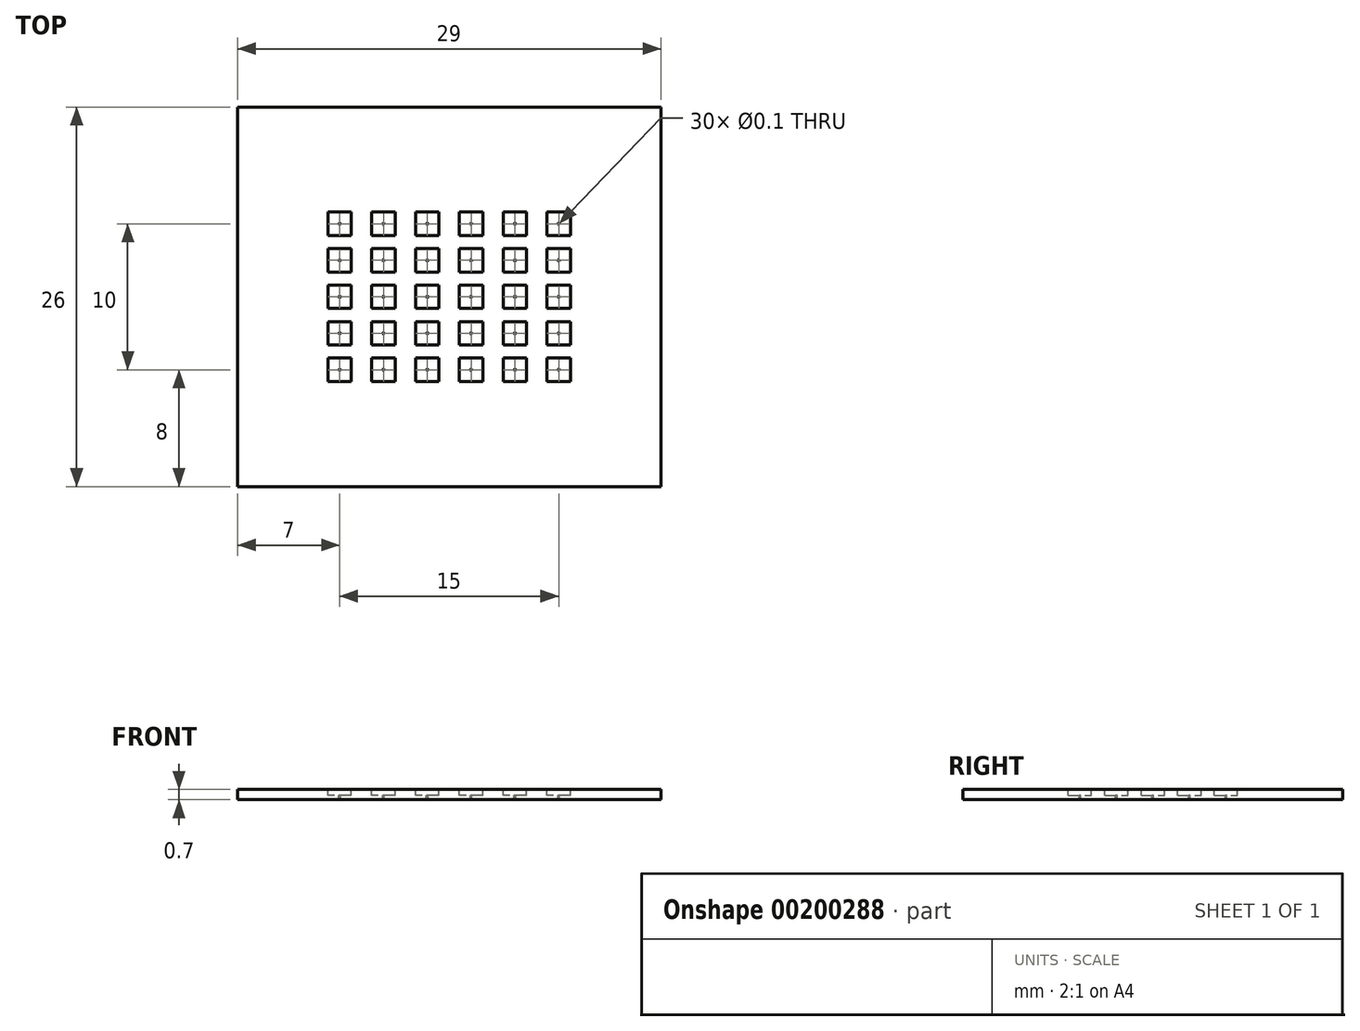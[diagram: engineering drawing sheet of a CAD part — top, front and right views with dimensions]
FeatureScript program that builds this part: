
annotation { "Feature Type Name" : "Feature", "Feature Type Description" : "" }
export const myFeature = defineFeature(function(context is Context, id is Id, definition is map)
    precondition{}
    {
        {
            var Q0;
            Q0=qCreatedBy(makeId("Top.planeOp"),FACE);
            var sketch = newSketch(context, id + "F0", { "sketchPlane" : qUnion([Q0])});
            skLineSegment(sketch, "E0.bottom", {"start": v(14.5, -13) * mm, "end": v(-14.5, -13) * mm});
            skLineSegment(sketch, "E0.top", {"start": v(14.5, 13) * mm, "end": v(-14.5, 13) * mm});
            skLineSegment(sketch, "E0.left", {"start": v(14.5, -13) * mm, "end": v(14.5, 13) * mm});
            skLineSegment(sketch, "E0.right", {"start": v(-14.5, -13) * mm, "end": v(-14.5, 13) * mm});
            skPoint(sketch, "E0.middle", {"position": v(0, 0) * mm});
            skSolve(sketch);
        }
        {
            var Q0;
            Q0=qSketchRegion(id+"F0",true);
            var Q1;
            Q1=makeQuery(id+"F0.imprint","IMPRINT",FACE,{"disambiguationData":[TD([[makeQuery(id+"F0.imprint","IMPRINT",EDGE,{"derivedFrom":sQuery(id+"F0.wireOp",EDGE,"UkhYZKIQ-UkVG-Lxvr-Lrxv-xQsFVOTcTfzZ.bottom")}),-1.0]])]});
            extrude(context, id + "F1", {"entities" : qUnion([Q0, Q1]), "oppositeDirection" : true, "depth" : 0.7 * mm});
        }
        {
            var Q0;
            Q0=makeQuery(id+"F1.opExtrude","CAP_FACE",FACE,{"disambiguationData":[OSD([sQuery(id+"F0.wireOp",EDGE,"E0.bottom"),sQuery(id+"F0.wireOp",EDGE,"E0.top"),sQuery(id+"F0.wireOp",EDGE,"E0.left"),sQuery(id+"F0.wireOp",EDGE,"E0.right")])],"isStart":true});
            var sketch = newSketch(context, id + "F2", { "sketchPlane" : qUnion([Q0])});
            skLineSegment(sketch, "E1.bottom", {"start": v(12.75, -11.25) * mm, "end": v(-12.75, -11.25) * mm});
            skLineSegment(sketch, "E1.top", {"start": v(12.75, 11.25) * mm, "end": v(-12.75, 11.25) * mm});
            skLineSegment(sketch, "E1.left", {"start": v(12.75, -11.25) * mm, "end": v(12.75, 11.25) * mm});
            skLineSegment(sketch, "E1.right", {"start": v(-12.75, -11.25) * mm, "end": v(-12.75, 11.25) * mm});
            skPoint(sketch, "E1.middle", {"position": v(0, 0) * mm});
            skLineSegment(sketch, "E2.bottom", {"start": v(13.25, -11.75) * mm, "end": v(-13.25, -11.75) * mm});
            skLineSegment(sketch, "E2.top", {"start": v(13.25, 11.75) * mm, "end": v(-13.25, 11.75) * mm});
            skLineSegment(sketch, "E2.left", {"start": v(13.25, -11.75) * mm, "end": v(13.25, 11.75) * mm});
            skLineSegment(sketch, "E2.right", {"start": v(-13.25, -11.75) * mm, "end": v(-13.25, 11.75) * mm});
            skSolve(sketch);
        }
        {
            var Q0;
            Q0=makeQuery(id+"FLxWal6u9J4FSth_1.boolean.opBoolean","SPLIT",FACE,{"disambiguationData":[TD([makeQuery(id+"FLxWal6u9J4FSth_1.opExtrude","SWEPT_FACE",FACE,{"disambiguationData":[OSD([sQuery(id+"F2.wireOp",EDGE,"E1.bottom")])]})])],"derivedFrom":makeQuery(id+"F1.opExtrude","CAP_FACE",FACE,{"disambiguationData":[OSD([sQuery(id+"F0.wireOp",EDGE,"E0.bottom"),sQuery(id+"F0.wireOp",EDGE,"E0.top"),sQuery(id+"F0.wireOp",EDGE,"E0.left"),sQuery(id+"F0.wireOp",EDGE,"E0.right")])],"isStart":true})});
            var sketch = newSketch(context, id + "F3", { "sketchPlane" : qUnion([Q0])});
            skPoint(sketch, "E3.middle", {"position": v(0, 0) * mm});
            skPoint(sketch, "E4", {"position": v(-7.5, 5) * mm});
            skPoint(sketch, "E5", {"position": v(-4.5, 5) * mm});
            skPoint(sketch, "E6", {"position": v(-1.5, 5) * mm});
            skPoint(sketch, "E7", {"position": v(1.5, 5) * mm});
            skPoint(sketch, "E8", {"position": v(4.5, 5) * mm});
            skPoint(sketch, "E9", {"position": v(7.5, 5) * mm});
            skPoint(sketch, "E10", {"position": v(-7.5, 2.5) * mm});
            skPoint(sketch, "E11", {"position": v(-4.5, 2.5) * mm});
            skPoint(sketch, "E12", {"position": v(-1.5, 2.5) * mm});
            skPoint(sketch, "E13", {"position": v(1.5, 2.5) * mm});
            skPoint(sketch, "E14", {"position": v(4.5, 2.5) * mm});
            skPoint(sketch, "E15", {"position": v(7.5, 2.5) * mm});
            skPoint(sketch, "E16", {"position": v(-7.5, 0) * mm});
            skPoint(sketch, "E17", {"position": v(-4.5, 0) * mm});
            skPoint(sketch, "E18", {"position": v(-1.5, 0) * mm});
            skPoint(sketch, "E19", {"position": v(1.5, 0) * mm});
            skPoint(sketch, "E20", {"position": v(4.5, 0) * mm});
            skPoint(sketch, "E21", {"position": v(7.5, 0) * mm});
            skPoint(sketch, "E22", {"position": v(-7.5, -2.5) * mm});
            skPoint(sketch, "E23", {"position": v(-4.5, -2.5) * mm});
            skPoint(sketch, "E24", {"position": v(-1.5, -2.5) * mm});
            skPoint(sketch, "E25", {"position": v(1.5, -2.5) * mm});
            skPoint(sketch, "E26", {"position": v(4.5, -2.5) * mm});
            skPoint(sketch, "E27", {"position": v(7.5, -2.5) * mm});
            skPoint(sketch, "E28", {"position": v(-7.5, -5) * mm});
            skPoint(sketch, "E29", {"position": v(-4.5, -5) * mm});
            skPoint(sketch, "E30", {"position": v(-1.5, -5) * mm});
            skPoint(sketch, "E31", {"position": v(1.5, -5) * mm});
            skPoint(sketch, "E32", {"position": v(4.5, -5) * mm});
            skPoint(sketch, "E33", {"position": v(7.5, -5) * mm});
            skLineSegment(sketch, "E34.bottom", {"start": v(-6.7, 4.2) * mm, "end": v(-8.3, 4.2) * mm});
            skLineSegment(sketch, "E34.top", {"start": v(-6.7, 5.8) * mm, "end": v(-8.3, 5.8) * mm});
            skLineSegment(sketch, "E34.left", {"start": v(-6.7, 4.2) * mm, "end": v(-6.7, 5.8) * mm});
            skLineSegment(sketch, "E34.right", {"start": v(-8.3, 4.2) * mm, "end": v(-8.3, 5.8) * mm});
            skLineSegment(sketch, "E35.bottom", {"start": v(-3.7, 4.2) * mm, "end": v(-5.3, 4.2) * mm});
            skLineSegment(sketch, "E35.top", {"start": v(-3.7, 5.8) * mm, "end": v(-5.3, 5.8) * mm});
            skLineSegment(sketch, "E35.left", {"start": v(-3.7, 4.2) * mm, "end": v(-3.7, 5.8) * mm});
            skLineSegment(sketch, "E35.right", {"start": v(-5.3, 4.2) * mm, "end": v(-5.3, 5.8) * mm});
            skLineSegment(sketch, "E36.bottom", {"start": v(-0.7, 4.2) * mm, "end": v(-2.3, 4.2) * mm});
            skLineSegment(sketch, "E36.top", {"start": v(-0.7, 5.8) * mm, "end": v(-2.3, 5.8) * mm});
            skLineSegment(sketch, "E36.left", {"start": v(-0.7, 4.2) * mm, "end": v(-0.7, 5.8) * mm});
            skLineSegment(sketch, "E36.right", {"start": v(-2.3, 4.2) * mm, "end": v(-2.3, 5.8) * mm});
            skLineSegment(sketch, "E37.bottom", {"start": v(2.3, 4.2) * mm, "end": v(0.7, 4.2) * mm});
            skLineSegment(sketch, "E37.top", {"start": v(2.3, 5.8) * mm, "end": v(0.7, 5.8) * mm});
            skLineSegment(sketch, "E37.left", {"start": v(2.3, 4.2) * mm, "end": v(2.3, 5.8) * mm});
            skLineSegment(sketch, "E37.right", {"start": v(0.7, 4.2) * mm, "end": v(0.7, 5.8) * mm});
            skLineSegment(sketch, "E38.bottom", {"start": v(5.3, 4.2) * mm, "end": v(3.7, 4.2) * mm});
            skLineSegment(sketch, "E38.top", {"start": v(5.3, 5.8) * mm, "end": v(3.7, 5.8) * mm});
            skLineSegment(sketch, "E38.left", {"start": v(5.3, 4.2) * mm, "end": v(5.3, 5.8) * mm});
            skLineSegment(sketch, "E38.right", {"start": v(3.7, 4.2) * mm, "end": v(3.7, 5.8) * mm});
            skLineSegment(sketch, "E39.bottom", {"start": v(8.3, 4.2) * mm, "end": v(6.7, 4.2) * mm});
            skLineSegment(sketch, "E39.top", {"start": v(8.3, 5.8) * mm, "end": v(6.7, 5.8) * mm});
            skLineSegment(sketch, "E39.left", {"start": v(8.3, 4.2) * mm, "end": v(8.3, 5.8) * mm});
            skLineSegment(sketch, "E39.right", {"start": v(6.7, 4.2) * mm, "end": v(6.7, 5.8) * mm});
            skLineSegment(sketch, "E40.bottom", {"start": v(-6.7, 1.7) * mm, "end": v(-8.3, 1.7) * mm});
            skLineSegment(sketch, "E40.top", {"start": v(-6.7, 3.3) * mm, "end": v(-8.3, 3.3) * mm});
            skLineSegment(sketch, "E40.left", {"start": v(-6.7, 1.7) * mm, "end": v(-6.7, 3.3) * mm});
            skLineSegment(sketch, "E40.right", {"start": v(-8.3, 1.7) * mm, "end": v(-8.3, 3.3) * mm});
            skLineSegment(sketch, "E41.bottom", {"start": v(-3.7, 1.7) * mm, "end": v(-5.3, 1.7) * mm});
            skLineSegment(sketch, "E41.top", {"start": v(-3.7, 3.3) * mm, "end": v(-5.3, 3.3) * mm});
            skLineSegment(sketch, "E41.left", {"start": v(-3.7, 1.7) * mm, "end": v(-3.7, 3.3) * mm});
            skLineSegment(sketch, "E41.right", {"start": v(-5.3, 1.7) * mm, "end": v(-5.3, 3.3) * mm});
            skLineSegment(sketch, "E42.bottom", {"start": v(-0.7, 1.7) * mm, "end": v(-2.3, 1.7) * mm});
            skLineSegment(sketch, "E42.top", {"start": v(-0.7, 3.3) * mm, "end": v(-2.3, 3.3) * mm});
            skLineSegment(sketch, "E42.left", {"start": v(-0.7, 1.7) * mm, "end": v(-0.7, 3.3) * mm});
            skLineSegment(sketch, "E42.right", {"start": v(-2.3, 1.7) * mm, "end": v(-2.3, 3.3) * mm});
            skLineSegment(sketch, "E43.bottom", {"start": v(2.3, 1.7) * mm, "end": v(0.7, 1.7) * mm});
            skLineSegment(sketch, "E43.top", {"start": v(2.3, 3.3) * mm, "end": v(0.7, 3.3) * mm});
            skLineSegment(sketch, "E43.left", {"start": v(2.3, 1.7) * mm, "end": v(2.3, 3.3) * mm});
            skLineSegment(sketch, "E43.right", {"start": v(0.7, 1.7) * mm, "end": v(0.7, 3.3) * mm});
            skLineSegment(sketch, "E44.bottom", {"start": v(5.3, 1.7) * mm, "end": v(3.7, 1.7) * mm});
            skLineSegment(sketch, "E44.top", {"start": v(5.3, 3.3) * mm, "end": v(3.7, 3.3) * mm});
            skLineSegment(sketch, "E44.left", {"start": v(5.3, 1.7) * mm, "end": v(5.3, 3.3) * mm});
            skLineSegment(sketch, "E44.right", {"start": v(3.7, 1.7) * mm, "end": v(3.7, 3.3) * mm});
            skLineSegment(sketch, "E45.bottom", {"start": v(8.3, 1.7) * mm, "end": v(6.7, 1.7) * mm});
            skLineSegment(sketch, "E45.top", {"start": v(8.3, 3.3) * mm, "end": v(6.7, 3.3) * mm});
            skLineSegment(sketch, "E45.left", {"start": v(8.3, 1.7) * mm, "end": v(8.3, 3.3) * mm});
            skLineSegment(sketch, "E45.right", {"start": v(6.7, 1.7) * mm, "end": v(6.7, 3.3) * mm});
            skLineSegment(sketch, "E46.bottom", {"start": v(-6.7, -0.8) * mm, "end": v(-8.3, -0.8) * mm});
            skLineSegment(sketch, "E46.top", {"start": v(-6.7, 0.8) * mm, "end": v(-8.3, 0.8) * mm});
            skLineSegment(sketch, "E46.left", {"start": v(-6.7, -0.8) * mm, "end": v(-6.7, 0.8) * mm});
            skLineSegment(sketch, "E46.right", {"start": v(-8.3, -0.8) * mm, "end": v(-8.3, 0.8) * mm});
            skLineSegment(sketch, "E47.bottom", {"start": v(-3.7, -0.8) * mm, "end": v(-5.3, -0.8) * mm});
            skLineSegment(sketch, "E47.top", {"start": v(-3.7, 0.8) * mm, "end": v(-5.3, 0.8) * mm});
            skLineSegment(sketch, "E47.left", {"start": v(-3.7, -0.8) * mm, "end": v(-3.7, 0.8) * mm});
            skLineSegment(sketch, "E47.right", {"start": v(-5.3, -0.8) * mm, "end": v(-5.3, 0.8) * mm});
            skLineSegment(sketch, "E48.bottom", {"start": v(-0.7, -0.8) * mm, "end": v(-2.3, -0.8) * mm});
            skLineSegment(sketch, "E48.top", {"start": v(-0.7, 0.8) * mm, "end": v(-2.3, 0.8) * mm});
            skLineSegment(sketch, "E48.left", {"start": v(-0.7, -0.8) * mm, "end": v(-0.7, 0.8) * mm});
            skLineSegment(sketch, "E48.right", {"start": v(-2.3, -0.8) * mm, "end": v(-2.3, 0.8) * mm});
            skLineSegment(sketch, "E49.bottom", {"start": v(2.3, -0.8) * mm, "end": v(0.7, -0.8) * mm});
            skLineSegment(sketch, "E49.top", {"start": v(2.3, 0.8) * mm, "end": v(0.7, 0.8) * mm});
            skLineSegment(sketch, "E49.left", {"start": v(2.3, -0.8) * mm, "end": v(2.3, 0.8) * mm});
            skLineSegment(sketch, "E49.right", {"start": v(0.7, -0.8) * mm, "end": v(0.7, 0.8) * mm});
            skLineSegment(sketch, "E50.bottom", {"start": v(5.3, -0.8) * mm, "end": v(3.7, -0.8) * mm});
            skLineSegment(sketch, "E50.top", {"start": v(5.3, 0.8) * mm, "end": v(3.7, 0.8) * mm});
            skLineSegment(sketch, "E50.left", {"start": v(5.3, -0.8) * mm, "end": v(5.3, 0.8) * mm});
            skLineSegment(sketch, "E50.right", {"start": v(3.7, -0.8) * mm, "end": v(3.7, 0.8) * mm});
            skLineSegment(sketch, "E51.bottom", {"start": v(8.3, -0.8) * mm, "end": v(6.7, -0.8) * mm});
            skLineSegment(sketch, "E51.top", {"start": v(8.3, 0.8) * mm, "end": v(6.7, 0.8) * mm});
            skLineSegment(sketch, "E51.left", {"start": v(8.3, -0.8) * mm, "end": v(8.3, 0.8) * mm});
            skLineSegment(sketch, "E51.right", {"start": v(6.7, -0.8) * mm, "end": v(6.7, 0.8) * mm});
            skLineSegment(sketch, "E52.bottom", {"start": v(-6.7, -3.3) * mm, "end": v(-8.3, -3.3) * mm});
            skLineSegment(sketch, "E52.top", {"start": v(-6.7, -1.7) * mm, "end": v(-8.3, -1.7) * mm});
            skLineSegment(sketch, "E52.left", {"start": v(-6.7, -3.3) * mm, "end": v(-6.7, -1.7) * mm});
            skLineSegment(sketch, "E52.right", {"start": v(-8.3, -3.3) * mm, "end": v(-8.3, -1.7) * mm});
            skLineSegment(sketch, "E53.bottom", {"start": v(-3.7, -3.3) * mm, "end": v(-5.3, -3.3) * mm});
            skLineSegment(sketch, "E53.top", {"start": v(-3.7, -1.7) * mm, "end": v(-5.3, -1.7) * mm});
            skLineSegment(sketch, "E53.left", {"start": v(-3.7, -3.3) * mm, "end": v(-3.7, -1.7) * mm});
            skLineSegment(sketch, "E53.right", {"start": v(-5.3, -3.3) * mm, "end": v(-5.3, -1.7) * mm});
            skLineSegment(sketch, "E54.bottom", {"start": v(-0.7, -3.3) * mm, "end": v(-2.3, -3.3) * mm});
            skLineSegment(sketch, "E54.top", {"start": v(-0.7, -1.7) * mm, "end": v(-2.3, -1.7) * mm});
            skLineSegment(sketch, "E54.left", {"start": v(-0.7, -3.3) * mm, "end": v(-0.7, -1.7) * mm});
            skLineSegment(sketch, "E54.right", {"start": v(-2.3, -3.3) * mm, "end": v(-2.3, -1.7) * mm});
            skLineSegment(sketch, "E55.bottom", {"start": v(2.3, -3.3) * mm, "end": v(0.7, -3.3) * mm});
            skLineSegment(sketch, "E55.top", {"start": v(2.3, -1.7) * mm, "end": v(0.7, -1.7) * mm});
            skLineSegment(sketch, "E55.left", {"start": v(2.3, -3.3) * mm, "end": v(2.3, -1.7) * mm});
            skLineSegment(sketch, "E55.right", {"start": v(0.7, -3.3) * mm, "end": v(0.7, -1.7) * mm});
            skLineSegment(sketch, "E56.bottom", {"start": v(5.3, -3.3) * mm, "end": v(3.7, -3.3) * mm});
            skLineSegment(sketch, "E56.top", {"start": v(5.3, -1.7) * mm, "end": v(3.7, -1.7) * mm});
            skLineSegment(sketch, "E56.left", {"start": v(5.3, -3.3) * mm, "end": v(5.3, -1.7) * mm});
            skLineSegment(sketch, "E56.right", {"start": v(3.7, -3.3) * mm, "end": v(3.7, -1.7) * mm});
            skLineSegment(sketch, "E57.bottom", {"start": v(8.3, -3.3) * mm, "end": v(6.7, -3.3) * mm});
            skLineSegment(sketch, "E57.top", {"start": v(8.3, -1.7) * mm, "end": v(6.7, -1.7) * mm});
            skLineSegment(sketch, "E57.left", {"start": v(8.3, -3.3) * mm, "end": v(8.3, -1.7) * mm});
            skLineSegment(sketch, "E57.right", {"start": v(6.7, -3.3) * mm, "end": v(6.7, -1.7) * mm});
            skLineSegment(sketch, "E58.bottom", {"start": v(-6.7, -5.8) * mm, "end": v(-8.3, -5.8) * mm});
            skLineSegment(sketch, "E58.top", {"start": v(-6.7, -4.2) * mm, "end": v(-8.3, -4.2) * mm});
            skLineSegment(sketch, "E58.left", {"start": v(-6.7, -5.8) * mm, "end": v(-6.7, -4.2) * mm});
            skLineSegment(sketch, "E58.right", {"start": v(-8.3, -5.8) * mm, "end": v(-8.3, -4.2) * mm});
            skLineSegment(sketch, "E59.bottom", {"start": v(-3.7, -5.8) * mm, "end": v(-5.3, -5.8) * mm});
            skLineSegment(sketch, "E59.top", {"start": v(-3.7, -4.2) * mm, "end": v(-5.3, -4.2) * mm});
            skLineSegment(sketch, "E59.left", {"start": v(-3.7, -5.8) * mm, "end": v(-3.7, -4.2) * mm});
            skLineSegment(sketch, "E59.right", {"start": v(-5.3, -5.8) * mm, "end": v(-5.3, -4.2) * mm});
            skLineSegment(sketch, "E60.bottom", {"start": v(-0.7, -5.8) * mm, "end": v(-2.3, -5.8) * mm});
            skLineSegment(sketch, "E60.top", {"start": v(-0.7, -4.2) * mm, "end": v(-2.3, -4.2) * mm});
            skLineSegment(sketch, "E60.left", {"start": v(-0.7, -5.8) * mm, "end": v(-0.7, -4.2) * mm});
            skLineSegment(sketch, "E60.right", {"start": v(-2.3, -5.8) * mm, "end": v(-2.3, -4.2) * mm});
            skLineSegment(sketch, "E61.bottom", {"start": v(2.3, -5.8) * mm, "end": v(0.7, -5.8) * mm});
            skLineSegment(sketch, "E61.top", {"start": v(2.3, -4.2) * mm, "end": v(0.7, -4.2) * mm});
            skLineSegment(sketch, "E61.left", {"start": v(2.3, -5.8) * mm, "end": v(2.3, -4.2) * mm});
            skLineSegment(sketch, "E61.right", {"start": v(0.7, -5.8) * mm, "end": v(0.7, -4.2) * mm});
            skLineSegment(sketch, "E62.bottom", {"start": v(5.3, -5.8) * mm, "end": v(3.7, -5.8) * mm});
            skLineSegment(sketch, "E62.top", {"start": v(5.3, -4.2) * mm, "end": v(3.7, -4.2) * mm});
            skLineSegment(sketch, "E62.left", {"start": v(5.3, -5.8) * mm, "end": v(5.3, -4.2) * mm});
            skLineSegment(sketch, "E62.right", {"start": v(3.7, -5.8) * mm, "end": v(3.7, -4.2) * mm});
            skLineSegment(sketch, "E63.bottom", {"start": v(8.3, -5.8) * mm, "end": v(6.7, -5.8) * mm});
            skLineSegment(sketch, "E63.top", {"start": v(8.3, -4.2) * mm, "end": v(6.7, -4.2) * mm});
            skLineSegment(sketch, "E63.left", {"start": v(8.3, -5.8) * mm, "end": v(8.3, -4.2) * mm});
            skLineSegment(sketch, "E63.right", {"start": v(6.7, -5.8) * mm, "end": v(6.7, -4.2) * mm});
            skSolve(sketch);
        }
        {
            var Q0;
            Q0=qSketchRegion(id+"F3",true);
            extrude(context, id + "F4", {"entities" : qUnion([Q0]), "operationType" : NewBodyOperationType.REMOVE, "oppositeDirection" : true, "depth" : 0.4 * mm, "offsetDistance" : 25 * mm});
        }
        {
            var Q0;
            Q0=makeQuery(id+"F4.boolean.opBoolean","COPY",FACE,{"derivedFrom":makeQuery(id+"F4.opExtrude","CAP_FACE",FACE,{"disambiguationData":[OSD([sQuery(id+"F3.wireOp",EDGE,"E34.bottom"),sQuery(id+"F3.wireOp",EDGE,"E34.top"),sQuery(id+"F3.wireOp",EDGE,"E34.left"),sQuery(id+"F3.wireOp",EDGE,"E34.right")])],"isStart":false})});
            var sketch = newSketch(context, id + "F5", { "sketchPlane" : qUnion([Q0])});
            skPoint(sketch, "E64", {"position": v(-7.5, 5) * mm});
            skSolve(sketch);
        }
        {
            var Q0;
            Q0=sQuery(id+"F5.wireOp",VERTEX,"E64");
            var Q1;
            Q1=makeQuery(id+"F1.opExtrude","SWEPT_BODY",BODY,{"disambiguationData":[OSD([sQuery(id+"F0.wireOp",EDGE,"E0.bottom"),sQuery(id+"F0.wireOp",EDGE,"E0.top"),sQuery(id+"F0.wireOp",EDGE,"E0.left"),sQuery(id+"F0.wireOp",EDGE,"E0.right")])]});
            hole(context, id + "F6", {"style" : HoleStyle.SIMPLE, "endStyle" : HoleEndStyle.THROUGH, "holeDiameter" : 0.1 * mm, "startFromSketch" : true, "locations" : qUnion([Q0]), "scope" : qUnion([Q1]), "isTappedThrough" : true});
        }
        {
            var Q0;
            Q0=makeQuery(id+"F4.boolean.opBoolean","COPY",FACE,{"derivedFrom":makeQuery(id+"F4.opExtrude","CAP_FACE",FACE,{"disambiguationData":[OSD([sQuery(id+"F3.wireOp",EDGE,"E35.bottom"),sQuery(id+"F3.wireOp",EDGE,"E35.top"),sQuery(id+"F3.wireOp",EDGE,"E35.left"),sQuery(id+"F3.wireOp",EDGE,"E35.right")])],"isStart":false})});
            var sketch = newSketch(context, id + "F7", { "sketchPlane" : qUnion([Q0])});
            skPoint(sketch, "E65", {"position": v(-4.5, 5) * mm});
            skSolve(sketch);
        }
        {
            var Q0;
            Q0=sQuery(id+"F7.wireOp",VERTEX,"E65");
            var Q1;
            Q1=makeQuery(id+"F1.opExtrude","SWEPT_BODY",BODY,{"disambiguationData":[OSD([sQuery(id+"F0.wireOp",EDGE,"E0.bottom"),sQuery(id+"F0.wireOp",EDGE,"E0.top"),sQuery(id+"F0.wireOp",EDGE,"E0.left"),sQuery(id+"F0.wireOp",EDGE,"E0.right")])]});
            hole(context, id + "F8", {"style" : HoleStyle.SIMPLE, "endStyle" : HoleEndStyle.THROUGH, "holeDiameter" : 0.1 * mm, "startFromSketch" : true, "locations" : qUnion([Q0]), "scope" : qUnion([Q1]), "isTappedThrough" : true});
        }
        {
            var Q0;
            Q0=makeQuery(id+"F4.boolean.opBoolean","COPY",FACE,{"derivedFrom":makeQuery(id+"F4.opExtrude","CAP_FACE",FACE,{"disambiguationData":[OSD([sQuery(id+"F3.wireOp",EDGE,"E36.bottom"),sQuery(id+"F3.wireOp",EDGE,"E36.top"),sQuery(id+"F3.wireOp",EDGE,"E36.left"),sQuery(id+"F3.wireOp",EDGE,"E36.right")])],"isStart":false})});
            var sketch = newSketch(context, id + "F9", { "sketchPlane" : qUnion([Q0])});
            skPoint(sketch, "E66", {"position": v(-1.5, 5) * mm});
            skSolve(sketch);
        }
        {
            var Q0;
            Q0=sQuery(id+"F9.wireOp",VERTEX,"E66");
            var Q1;
            Q1=makeQuery(id+"F1.opExtrude","SWEPT_BODY",BODY,{"disambiguationData":[OSD([sQuery(id+"F0.wireOp",EDGE,"E0.bottom"),sQuery(id+"F0.wireOp",EDGE,"E0.top"),sQuery(id+"F0.wireOp",EDGE,"E0.left"),sQuery(id+"F0.wireOp",EDGE,"E0.right")])]});
            hole(context, id + "F10", {"style" : HoleStyle.SIMPLE, "endStyle" : HoleEndStyle.THROUGH, "holeDiameter" : 0.1 * mm, "startFromSketch" : true, "locations" : qUnion([Q0]), "scope" : qUnion([Q1]), "isTappedThrough" : true});
        }
        {
            var Q0;
            Q0=makeQuery(id+"F4.boolean.opBoolean","COPY",FACE,{"derivedFrom":makeQuery(id+"F4.opExtrude","CAP_FACE",FACE,{"disambiguationData":[OSD([sQuery(id+"F3.wireOp",EDGE,"E37.bottom"),sQuery(id+"F3.wireOp",EDGE,"E37.top"),sQuery(id+"F3.wireOp",EDGE,"E37.left"),sQuery(id+"F3.wireOp",EDGE,"E37.right")])],"isStart":false})});
            var sketch = newSketch(context, id + "F11", { "sketchPlane" : qUnion([Q0])});
            skPoint(sketch, "E67", {"position": v(1.5, 5) * mm});
            skSolve(sketch);
        }
        {
            var Q0;
            Q0=sQuery(id+"F11.wireOp",VERTEX,"E67");
            var Q1;
            Q1=makeQuery(id+"F1.opExtrude","SWEPT_BODY",BODY,{"disambiguationData":[OSD([sQuery(id+"F0.wireOp",EDGE,"E0.bottom"),sQuery(id+"F0.wireOp",EDGE,"E0.top"),sQuery(id+"F0.wireOp",EDGE,"E0.left"),sQuery(id+"F0.wireOp",EDGE,"E0.right")])]});
            hole(context, id + "F12", {"style" : HoleStyle.SIMPLE, "endStyle" : HoleEndStyle.THROUGH, "holeDiameter" : 0.1 * mm, "startFromSketch" : true, "locations" : qUnion([Q0]), "scope" : qUnion([Q1]), "isTappedThrough" : true});
        }
        {
            var Q0;
            Q0=makeQuery(id+"F4.boolean.opBoolean","COPY",FACE,{"derivedFrom":makeQuery(id+"F4.opExtrude","CAP_FACE",FACE,{"disambiguationData":[OSD([sQuery(id+"F3.wireOp",EDGE,"E38.bottom"),sQuery(id+"F3.wireOp",EDGE,"E38.top"),sQuery(id+"F3.wireOp",EDGE,"E38.left"),sQuery(id+"F3.wireOp",EDGE,"E38.right")])],"isStart":false})});
            var sketch = newSketch(context, id + "F13", { "sketchPlane" : qUnion([Q0])});
            skPoint(sketch, "E68", {"position": v(4.5, 5) * mm});
            skSolve(sketch);
        }
        {
            var Q0;
            Q0=sQuery(id+"F13.wireOp",VERTEX,"E68");
            var Q1;
            Q1=makeQuery(id+"F1.opExtrude","SWEPT_BODY",BODY,{"disambiguationData":[OSD([sQuery(id+"F0.wireOp",EDGE,"E0.bottom"),sQuery(id+"F0.wireOp",EDGE,"E0.top"),sQuery(id+"F0.wireOp",EDGE,"E0.left"),sQuery(id+"F0.wireOp",EDGE,"E0.right")])]});
            hole(context, id + "F14", {"style" : HoleStyle.SIMPLE, "endStyle" : HoleEndStyle.THROUGH, "holeDiameter" : 0.1 * mm, "startFromSketch" : true, "locations" : qUnion([Q0]), "scope" : qUnion([Q1]), "isTappedThrough" : true});
        }
        {
            var Q0;
            Q0=makeQuery(id+"F4.boolean.opBoolean","COPY",FACE,{"derivedFrom":makeQuery(id+"F4.opExtrude","CAP_FACE",FACE,{"disambiguationData":[OSD([sQuery(id+"F3.wireOp",EDGE,"E39.bottom"),sQuery(id+"F3.wireOp",EDGE,"E39.top"),sQuery(id+"F3.wireOp",EDGE,"E39.left"),sQuery(id+"F3.wireOp",EDGE,"E39.right")])],"isStart":false})});
            var sketch = newSketch(context, id + "F15", { "sketchPlane" : qUnion([Q0])});
            skPoint(sketch, "E69", {"position": v(7.5, 5) * mm});
            skSolve(sketch);
        }
        {
            var Q0;
            Q0=sQuery(id+"F15.wireOp",VERTEX,"E69");
            var Q1;
            Q1=makeQuery(id+"F1.opExtrude","SWEPT_BODY",BODY,{"disambiguationData":[OSD([sQuery(id+"F0.wireOp",EDGE,"E0.bottom"),sQuery(id+"F0.wireOp",EDGE,"E0.top"),sQuery(id+"F0.wireOp",EDGE,"E0.left"),sQuery(id+"F0.wireOp",EDGE,"E0.right")])]});
            hole(context, id + "F16", {"style" : HoleStyle.SIMPLE, "endStyle" : HoleEndStyle.THROUGH, "holeDiameter" : 0.1 * mm, "startFromSketch" : true, "locations" : qUnion([Q0]), "scope" : qUnion([Q1]), "isTappedThrough" : true});
        }
        {
            var Q0;
            Q0=makeQuery(id+"F4.boolean.opBoolean","COPY",FACE,{"derivedFrom":makeQuery(id+"F4.opExtrude","CAP_FACE",FACE,{"disambiguationData":[OSD([sQuery(id+"F3.wireOp",EDGE,"E45.bottom"),sQuery(id+"F3.wireOp",EDGE,"E45.top"),sQuery(id+"F3.wireOp",EDGE,"E45.left"),sQuery(id+"F3.wireOp",EDGE,"E45.right")])],"isStart":false})});
            var sketch = newSketch(context, id + "F17", { "sketchPlane" : qUnion([Q0])});
            skPoint(sketch, "E70", {"position": v(7.5, 2.5) * mm});
            skSolve(sketch);
        }
        {
            var Q0;
            Q0=sQuery(id+"F17.wireOp",VERTEX,"E70");
            var Q1;
            Q1=makeQuery(id+"F1.opExtrude","SWEPT_BODY",BODY,{"disambiguationData":[OSD([sQuery(id+"F0.wireOp",EDGE,"E0.bottom"),sQuery(id+"F0.wireOp",EDGE,"E0.top"),sQuery(id+"F0.wireOp",EDGE,"E0.left"),sQuery(id+"F0.wireOp",EDGE,"E0.right")])]});
            hole(context, id + "F18", {"style" : HoleStyle.SIMPLE, "endStyle" : HoleEndStyle.THROUGH, "holeDiameter" : 0.1 * mm, "startFromSketch" : true, "locations" : qUnion([Q0]), "scope" : qUnion([Q1]), "isTappedThrough" : true});
        }
        {
            var Q0;
            Q0=makeQuery(id+"F4.boolean.opBoolean","COPY",FACE,{"derivedFrom":makeQuery(id+"F4.opExtrude","CAP_FACE",FACE,{"disambiguationData":[OSD([sQuery(id+"F3.wireOp",EDGE,"E44.bottom"),sQuery(id+"F3.wireOp",EDGE,"E44.top"),sQuery(id+"F3.wireOp",EDGE,"E44.left"),sQuery(id+"F3.wireOp",EDGE,"E44.right")])],"isStart":false})});
            var sketch = newSketch(context, id + "F19", { "sketchPlane" : qUnion([Q0])});
            skPoint(sketch, "E71", {"position": v(4.5, 2.5) * mm});
            skSolve(sketch);
        }
        {
            var Q0;
            Q0=sQuery(id+"F19.wireOp",VERTEX,"E71");
            var Q1;
            Q1=makeQuery(id+"F1.opExtrude","SWEPT_BODY",BODY,{"disambiguationData":[OSD([sQuery(id+"F0.wireOp",EDGE,"E0.bottom"),sQuery(id+"F0.wireOp",EDGE,"E0.top"),sQuery(id+"F0.wireOp",EDGE,"E0.left"),sQuery(id+"F0.wireOp",EDGE,"E0.right")])]});
            hole(context, id + "F20", {"style" : HoleStyle.SIMPLE, "endStyle" : HoleEndStyle.THROUGH, "holeDiameter" : 0.1 * mm, "startFromSketch" : true, "locations" : qUnion([Q0]), "scope" : qUnion([Q1]), "isTappedThrough" : true});
        }
        {
            var Q0;
            Q0=makeQuery(id+"F4.boolean.opBoolean","COPY",FACE,{"derivedFrom":makeQuery(id+"F4.opExtrude","CAP_FACE",FACE,{"disambiguationData":[OSD([sQuery(id+"F3.wireOp",EDGE,"E43.bottom"),sQuery(id+"F3.wireOp",EDGE,"E43.top"),sQuery(id+"F3.wireOp",EDGE,"E43.left"),sQuery(id+"F3.wireOp",EDGE,"E43.right")])],"isStart":false})});
            var sketch = newSketch(context, id + "F21", { "sketchPlane" : qUnion([Q0])});
            skPoint(sketch, "E72", {"position": v(1.5, 2.5) * mm});
            skSolve(sketch);
        }
        {
            var Q0;
            Q0=sQuery(id+"F21.wireOp",VERTEX,"E72");
            var Q1;
            Q1=makeQuery(id+"F1.opExtrude","SWEPT_BODY",BODY,{"disambiguationData":[OSD([sQuery(id+"F0.wireOp",EDGE,"E0.bottom"),sQuery(id+"F0.wireOp",EDGE,"E0.top"),sQuery(id+"F0.wireOp",EDGE,"E0.left"),sQuery(id+"F0.wireOp",EDGE,"E0.right")])]});
            hole(context, id + "F22", {"style" : HoleStyle.SIMPLE, "endStyle" : HoleEndStyle.THROUGH, "holeDiameter" : 0.1 * mm, "startFromSketch" : true, "locations" : qUnion([Q0]), "scope" : qUnion([Q1]), "isTappedThrough" : true});
        }
        {
            var Q0;
            Q0=makeQuery(id+"F4.boolean.opBoolean","COPY",FACE,{"derivedFrom":makeQuery(id+"F4.opExtrude","CAP_FACE",FACE,{"disambiguationData":[OSD([sQuery(id+"F3.wireOp",EDGE,"E42.bottom"),sQuery(id+"F3.wireOp",EDGE,"E42.top"),sQuery(id+"F3.wireOp",EDGE,"E42.left"),sQuery(id+"F3.wireOp",EDGE,"E42.right")])],"isStart":false})});
            var sketch = newSketch(context, id + "F23", { "sketchPlane" : qUnion([Q0])});
            skPoint(sketch, "E73", {"position": v(-1.5, 2.5) * mm});
            skSolve(sketch);
        }
        {
            var Q0;
            Q0=sQuery(id+"F23.wireOp",VERTEX,"E73");
            var Q1;
            Q1=makeQuery(id+"F1.opExtrude","SWEPT_BODY",BODY,{"disambiguationData":[OSD([sQuery(id+"F0.wireOp",EDGE,"E0.bottom"),sQuery(id+"F0.wireOp",EDGE,"E0.top"),sQuery(id+"F0.wireOp",EDGE,"E0.left"),sQuery(id+"F0.wireOp",EDGE,"E0.right")])]});
            hole(context, id + "F24", {"style" : HoleStyle.SIMPLE, "endStyle" : HoleEndStyle.THROUGH, "holeDiameter" : 0.1 * mm, "startFromSketch" : true, "locations" : qUnion([Q0]), "scope" : qUnion([Q1]), "isTappedThrough" : true});
        }
        {
            var Q0;
            Q0=makeQuery(id+"F4.boolean.opBoolean","COPY",FACE,{"derivedFrom":makeQuery(id+"F4.opExtrude","CAP_FACE",FACE,{"disambiguationData":[OSD([sQuery(id+"F3.wireOp",EDGE,"E41.bottom"),sQuery(id+"F3.wireOp",EDGE,"E41.top"),sQuery(id+"F3.wireOp",EDGE,"E41.left"),sQuery(id+"F3.wireOp",EDGE,"E41.right")])],"isStart":false})});
            var sketch = newSketch(context, id + "F25", { "sketchPlane" : qUnion([Q0])});
            skPoint(sketch, "E74", {"position": v(-4.5, 2.5) * mm});
            skSolve(sketch);
        }
        {
            var Q0;
            Q0=sQuery(id+"F25.wireOp",VERTEX,"E74");
            var Q1;
            Q1=makeQuery(id+"F1.opExtrude","SWEPT_BODY",BODY,{"disambiguationData":[OSD([sQuery(id+"F0.wireOp",EDGE,"E0.bottom"),sQuery(id+"F0.wireOp",EDGE,"E0.top"),sQuery(id+"F0.wireOp",EDGE,"E0.left"),sQuery(id+"F0.wireOp",EDGE,"E0.right")])]});
            hole(context, id + "F26", {"style" : HoleStyle.SIMPLE, "endStyle" : HoleEndStyle.THROUGH, "holeDiameter" : 0.1 * mm, "startFromSketch" : true, "locations" : qUnion([Q0]), "scope" : qUnion([Q1]), "isTappedThrough" : true});
        }
        {
            var Q0;
            Q0=makeQuery(id+"F4.boolean.opBoolean","COPY",FACE,{"derivedFrom":makeQuery(id+"F4.opExtrude","CAP_FACE",FACE,{"disambiguationData":[OSD([sQuery(id+"F3.wireOp",EDGE,"E40.bottom"),sQuery(id+"F3.wireOp",EDGE,"E40.top"),sQuery(id+"F3.wireOp",EDGE,"E40.left"),sQuery(id+"F3.wireOp",EDGE,"E40.right")])],"isStart":false})});
            var sketch = newSketch(context, id + "F27", { "sketchPlane" : qUnion([Q0])});
            skPoint(sketch, "E75", {"position": v(-7.5, 2.5) * mm});
            skSolve(sketch);
        }
        {
            var Q0;
            Q0=sQuery(id+"F27.wireOp",VERTEX,"E75");
            var Q1;
            Q1=makeQuery(id+"F1.opExtrude","SWEPT_BODY",BODY,{"disambiguationData":[OSD([sQuery(id+"F0.wireOp",EDGE,"E0.bottom"),sQuery(id+"F0.wireOp",EDGE,"E0.top"),sQuery(id+"F0.wireOp",EDGE,"E0.left"),sQuery(id+"F0.wireOp",EDGE,"E0.right")])]});
            hole(context, id + "F28", {"style" : HoleStyle.SIMPLE, "endStyle" : HoleEndStyle.THROUGH, "holeDiameter" : 0.1 * mm, "startFromSketch" : true, "locations" : qUnion([Q0]), "scope" : qUnion([Q1]), "isTappedThrough" : true});
        }
        {
            var Q0;
            Q0=makeQuery(id+"F4.boolean.opBoolean","COPY",FACE,{"derivedFrom":makeQuery(id+"F4.opExtrude","CAP_FACE",FACE,{"disambiguationData":[OSD([sQuery(id+"F3.wireOp",EDGE,"E46.bottom"),sQuery(id+"F3.wireOp",EDGE,"E46.top"),sQuery(id+"F3.wireOp",EDGE,"E46.left"),sQuery(id+"F3.wireOp",EDGE,"E46.right")])],"isStart":false})});
            var sketch = newSketch(context, id + "F29", { "sketchPlane" : qUnion([Q0])});
            skPoint(sketch, "E76", {"position": v(-7.5, 0) * mm});
            skSolve(sketch);
        }
        {
            var Q0;
            Q0=sQuery(id+"F29.wireOp",VERTEX,"E76");
            var Q1;
            Q1=makeQuery(id+"F1.opExtrude","SWEPT_BODY",BODY,{"disambiguationData":[OSD([sQuery(id+"F0.wireOp",EDGE,"E0.bottom"),sQuery(id+"F0.wireOp",EDGE,"E0.top"),sQuery(id+"F0.wireOp",EDGE,"E0.left"),sQuery(id+"F0.wireOp",EDGE,"E0.right")])]});
            hole(context, id + "F30", {"style" : HoleStyle.SIMPLE, "endStyle" : HoleEndStyle.THROUGH, "holeDiameter" : 0.1 * mm, "startFromSketch" : true, "locations" : qUnion([Q0]), "scope" : qUnion([Q1]), "isTappedThrough" : true});
        }
        {
            var Q0;
            Q0=makeQuery(id+"F4.boolean.opBoolean","COPY",FACE,{"derivedFrom":makeQuery(id+"F4.opExtrude","CAP_FACE",FACE,{"disambiguationData":[OSD([sQuery(id+"F3.wireOp",EDGE,"E47.bottom"),sQuery(id+"F3.wireOp",EDGE,"E47.top"),sQuery(id+"F3.wireOp",EDGE,"E47.left"),sQuery(id+"F3.wireOp",EDGE,"E47.right")])],"isStart":false})});
            var sketch = newSketch(context, id + "F31", { "sketchPlane" : qUnion([Q0])});
            skPoint(sketch, "E77", {"position": v(-4.5, 0) * mm});
            skSolve(sketch);
        }
        {
            var Q0;
            Q0=sQuery(id+"F31.wireOp",VERTEX,"E77");
            var Q1;
            Q1=makeQuery(id+"F1.opExtrude","SWEPT_BODY",BODY,{"disambiguationData":[OSD([sQuery(id+"F0.wireOp",EDGE,"E0.bottom"),sQuery(id+"F0.wireOp",EDGE,"E0.top"),sQuery(id+"F0.wireOp",EDGE,"E0.left"),sQuery(id+"F0.wireOp",EDGE,"E0.right")])]});
            hole(context, id + "F32", {"style" : HoleStyle.SIMPLE, "endStyle" : HoleEndStyle.THROUGH, "holeDiameter" : 0.1 * mm, "startFromSketch" : true, "locations" : qUnion([Q0]), "scope" : qUnion([Q1]), "isTappedThrough" : true});
        }
        {
            var Q0;
            Q0=makeQuery(id+"F4.boolean.opBoolean","COPY",FACE,{"derivedFrom":makeQuery(id+"F4.opExtrude","CAP_FACE",FACE,{"disambiguationData":[OSD([sQuery(id+"F3.wireOp",EDGE,"E48.bottom"),sQuery(id+"F3.wireOp",EDGE,"E48.top"),sQuery(id+"F3.wireOp",EDGE,"E48.left"),sQuery(id+"F3.wireOp",EDGE,"E48.right")])],"isStart":false})});
            var sketch = newSketch(context, id + "F33", { "sketchPlane" : qUnion([Q0])});
            skPoint(sketch, "E78", {"position": v(-1.5, 0) * mm});
            skSolve(sketch);
        }
        {
            var Q0;
            Q0=sQuery(id+"F33.wireOp",VERTEX,"E78");
            var Q1;
            Q1=makeQuery(id+"F1.opExtrude","SWEPT_BODY",BODY,{"disambiguationData":[OSD([sQuery(id+"F0.wireOp",EDGE,"E0.bottom"),sQuery(id+"F0.wireOp",EDGE,"E0.top"),sQuery(id+"F0.wireOp",EDGE,"E0.left"),sQuery(id+"F0.wireOp",EDGE,"E0.right")])]});
            hole(context, id + "F34", {"style" : HoleStyle.SIMPLE, "endStyle" : HoleEndStyle.THROUGH, "holeDiameter" : 0.1 * mm, "startFromSketch" : true, "locations" : qUnion([Q0]), "scope" : qUnion([Q1]), "isTappedThrough" : true});
        }
        {
            var Q0;
            Q0=makeQuery(id+"F4.boolean.opBoolean","COPY",FACE,{"derivedFrom":makeQuery(id+"F4.opExtrude","CAP_FACE",FACE,{"disambiguationData":[OSD([sQuery(id+"F3.wireOp",EDGE,"E49.bottom"),sQuery(id+"F3.wireOp",EDGE,"E49.top"),sQuery(id+"F3.wireOp",EDGE,"E49.left"),sQuery(id+"F3.wireOp",EDGE,"E49.right")])],"isStart":false})});
            var sketch = newSketch(context, id + "F35", { "sketchPlane" : qUnion([Q0])});
            skPoint(sketch, "E79", {"position": v(1.5, 0) * mm});
            skSolve(sketch);
        }
        {
            var Q0;
            Q0=sQuery(id+"F35.wireOp",VERTEX,"E79");
            var Q1;
            Q1=makeQuery(id+"F1.opExtrude","SWEPT_BODY",BODY,{"disambiguationData":[OSD([sQuery(id+"F0.wireOp",EDGE,"E0.bottom"),sQuery(id+"F0.wireOp",EDGE,"E0.top"),sQuery(id+"F0.wireOp",EDGE,"E0.left"),sQuery(id+"F0.wireOp",EDGE,"E0.right")])]});
            hole(context, id + "F36", {"style" : HoleStyle.SIMPLE, "endStyle" : HoleEndStyle.THROUGH, "holeDiameter" : 0.1 * mm, "startFromSketch" : true, "locations" : qUnion([Q0]), "scope" : qUnion([Q1]), "isTappedThrough" : true});
        }
        {
            var Q0;
            Q0=makeQuery(id+"F4.boolean.opBoolean","COPY",FACE,{"derivedFrom":makeQuery(id+"F4.opExtrude","CAP_FACE",FACE,{"disambiguationData":[OSD([sQuery(id+"F3.wireOp",EDGE,"E50.bottom"),sQuery(id+"F3.wireOp",EDGE,"E50.top"),sQuery(id+"F3.wireOp",EDGE,"E50.left"),sQuery(id+"F3.wireOp",EDGE,"E50.right")])],"isStart":false})});
            var sketch = newSketch(context, id + "F37", { "sketchPlane" : qUnion([Q0])});
            skPoint(sketch, "E80", {"position": v(4.5, 0) * mm});
            skSolve(sketch);
        }
        {
            var Q0;
            Q0=sQuery(id+"F37.wireOp",VERTEX,"E80");
            var Q1;
            Q1=makeQuery(id+"F1.opExtrude","SWEPT_BODY",BODY,{"disambiguationData":[OSD([sQuery(id+"F0.wireOp",EDGE,"E0.bottom"),sQuery(id+"F0.wireOp",EDGE,"E0.top"),sQuery(id+"F0.wireOp",EDGE,"E0.left"),sQuery(id+"F0.wireOp",EDGE,"E0.right")])]});
            hole(context, id + "F38", {"style" : HoleStyle.SIMPLE, "endStyle" : HoleEndStyle.THROUGH, "holeDiameter" : 0.1 * mm, "startFromSketch" : true, "locations" : qUnion([Q0]), "scope" : qUnion([Q1]), "isTappedThrough" : true});
        }
        {
            var Q0;
            Q0=makeQuery(id+"F4.boolean.opBoolean","COPY",FACE,{"derivedFrom":makeQuery(id+"F4.opExtrude","CAP_FACE",FACE,{"disambiguationData":[OSD([sQuery(id+"F3.wireOp",EDGE,"E51.bottom"),sQuery(id+"F3.wireOp",EDGE,"E51.top"),sQuery(id+"F3.wireOp",EDGE,"E51.left"),sQuery(id+"F3.wireOp",EDGE,"E51.right")])],"isStart":false})});
            var sketch = newSketch(context, id + "F39", { "sketchPlane" : qUnion([Q0])});
            skPoint(sketch, "E81", {"position": v(7.5, 0) * mm});
            skSolve(sketch);
        }
        {
            var Q0;
            Q0=sQuery(id+"F39.wireOp",VERTEX,"E81");
            var Q1;
            Q1=makeQuery(id+"F1.opExtrude","SWEPT_BODY",BODY,{"disambiguationData":[OSD([sQuery(id+"F0.wireOp",EDGE,"E0.bottom"),sQuery(id+"F0.wireOp",EDGE,"E0.top"),sQuery(id+"F0.wireOp",EDGE,"E0.left"),sQuery(id+"F0.wireOp",EDGE,"E0.right")])]});
            hole(context, id + "F40", {"style" : HoleStyle.SIMPLE, "endStyle" : HoleEndStyle.THROUGH, "holeDiameter" : 0.1 * mm, "startFromSketch" : true, "locations" : qUnion([Q0]), "scope" : qUnion([Q1]), "isTappedThrough" : true});
        }
        {
            var Q0;
            Q0=makeQuery(id+"F4.boolean.opBoolean","COPY",FACE,{"derivedFrom":makeQuery(id+"F4.opExtrude","CAP_FACE",FACE,{"disambiguationData":[OSD([sQuery(id+"F3.wireOp",EDGE,"E52.bottom"),sQuery(id+"F3.wireOp",EDGE,"E52.top"),sQuery(id+"F3.wireOp",EDGE,"E52.left"),sQuery(id+"F3.wireOp",EDGE,"E52.right")])],"isStart":false})});
            var sketch = newSketch(context, id + "F41", { "sketchPlane" : qUnion([Q0])});
            skPoint(sketch, "E82", {"position": v(-7.5, -2.5) * mm});
            skSolve(sketch);
        }
        {
            var Q0;
            Q0=sQuery(id+"F41.wireOp",VERTEX,"E82");
            var Q1;
            Q1=makeQuery(id+"F1.opExtrude","SWEPT_BODY",BODY,{"disambiguationData":[OSD([sQuery(id+"F0.wireOp",EDGE,"E0.bottom"),sQuery(id+"F0.wireOp",EDGE,"E0.top"),sQuery(id+"F0.wireOp",EDGE,"E0.left"),sQuery(id+"F0.wireOp",EDGE,"E0.right")])]});
            hole(context, id + "F42", {"style" : HoleStyle.SIMPLE, "endStyle" : HoleEndStyle.THROUGH, "holeDiameter" : 0.1 * mm, "startFromSketch" : true, "locations" : qUnion([Q0]), "scope" : qUnion([Q1]), "isTappedThrough" : true});
        }
        {
            var Q0;
            Q0=makeQuery(id+"F4.boolean.opBoolean","COPY",FACE,{"derivedFrom":makeQuery(id+"F4.opExtrude","CAP_FACE",FACE,{"disambiguationData":[OSD([sQuery(id+"F3.wireOp",EDGE,"E53.bottom"),sQuery(id+"F3.wireOp",EDGE,"E53.top"),sQuery(id+"F3.wireOp",EDGE,"E53.left"),sQuery(id+"F3.wireOp",EDGE,"E53.right")])],"isStart":false})});
            var sketch = newSketch(context, id + "F43", { "sketchPlane" : qUnion([Q0])});
            skPoint(sketch, "E83", {"position": v(-4.5, -2.5) * mm});
            skSolve(sketch);
        }
        {
            var Q0;
            Q0=sQuery(id+"F43.wireOp",VERTEX,"E83");
            var Q1;
            Q1=makeQuery(id+"F1.opExtrude","SWEPT_BODY",BODY,{"disambiguationData":[OSD([sQuery(id+"F0.wireOp",EDGE,"E0.bottom"),sQuery(id+"F0.wireOp",EDGE,"E0.top"),sQuery(id+"F0.wireOp",EDGE,"E0.left"),sQuery(id+"F0.wireOp",EDGE,"E0.right")])]});
            hole(context, id + "F44", {"style" : HoleStyle.SIMPLE, "endStyle" : HoleEndStyle.THROUGH, "holeDiameter" : 0.1 * mm, "startFromSketch" : true, "locations" : qUnion([Q0]), "scope" : qUnion([Q1]), "isTappedThrough" : true});
        }
        {
            var Q0;
            Q0=makeQuery(id+"F4.boolean.opBoolean","COPY",FACE,{"derivedFrom":makeQuery(id+"F4.opExtrude","CAP_FACE",FACE,{"disambiguationData":[OSD([sQuery(id+"F3.wireOp",EDGE,"E54.bottom"),sQuery(id+"F3.wireOp",EDGE,"E54.top"),sQuery(id+"F3.wireOp",EDGE,"E54.left"),sQuery(id+"F3.wireOp",EDGE,"E54.right")])],"isStart":false})});
            var sketch = newSketch(context, id + "F45", { "sketchPlane" : qUnion([Q0])});
            skPoint(sketch, "E84", {"position": v(-1.5, -2.5) * mm});
            skSolve(sketch);
        }
        {
            var Q0;
            Q0=sQuery(id+"F45.wireOp",VERTEX,"E84");
            var Q1;
            Q1=makeQuery(id+"F1.opExtrude","SWEPT_BODY",BODY,{"disambiguationData":[OSD([sQuery(id+"F0.wireOp",EDGE,"E0.bottom"),sQuery(id+"F0.wireOp",EDGE,"E0.top"),sQuery(id+"F0.wireOp",EDGE,"E0.left"),sQuery(id+"F0.wireOp",EDGE,"E0.right")])]});
            hole(context, id + "F46", {"style" : HoleStyle.SIMPLE, "endStyle" : HoleEndStyle.THROUGH, "holeDiameter" : 0.1 * mm, "startFromSketch" : true, "locations" : qUnion([Q0]), "scope" : qUnion([Q1]), "isTappedThrough" : true});
        }
        {
            var Q0;
            Q0=makeQuery(id+"F4.boolean.opBoolean","COPY",FACE,{"derivedFrom":makeQuery(id+"F4.opExtrude","CAP_FACE",FACE,{"disambiguationData":[OSD([sQuery(id+"F3.wireOp",EDGE,"E55.bottom"),sQuery(id+"F3.wireOp",EDGE,"E55.top"),sQuery(id+"F3.wireOp",EDGE,"E55.left"),sQuery(id+"F3.wireOp",EDGE,"E55.right")])],"isStart":false})});
            var sketch = newSketch(context, id + "F47", { "sketchPlane" : qUnion([Q0])});
            skPoint(sketch, "E85", {"position": v(1.5, -2.5) * mm});
            skSolve(sketch);
        }
        {
            var Q0;
            Q0=sQuery(id+"F47.wireOp",VERTEX,"E85");
            var Q1;
            Q1=makeQuery(id+"F1.opExtrude","SWEPT_BODY",BODY,{"disambiguationData":[OSD([sQuery(id+"F0.wireOp",EDGE,"E0.bottom"),sQuery(id+"F0.wireOp",EDGE,"E0.top"),sQuery(id+"F0.wireOp",EDGE,"E0.left"),sQuery(id+"F0.wireOp",EDGE,"E0.right")])]});
            hole(context, id + "F48", {"style" : HoleStyle.SIMPLE, "endStyle" : HoleEndStyle.THROUGH, "holeDiameter" : 0.1 * mm, "startFromSketch" : true, "locations" : qUnion([Q0]), "scope" : qUnion([Q1]), "isTappedThrough" : true});
        }
        {
            var Q0;
            Q0=makeQuery(id+"F4.boolean.opBoolean","COPY",FACE,{"derivedFrom":makeQuery(id+"F4.opExtrude","CAP_FACE",FACE,{"disambiguationData":[OSD([sQuery(id+"F3.wireOp",EDGE,"E56.bottom"),sQuery(id+"F3.wireOp",EDGE,"E56.top"),sQuery(id+"F3.wireOp",EDGE,"E56.left"),sQuery(id+"F3.wireOp",EDGE,"E56.right")])],"isStart":false})});
            var sketch = newSketch(context, id + "F49", { "sketchPlane" : qUnion([Q0])});
            skPoint(sketch, "E86", {"position": v(4.5, -2.5) * mm});
            skSolve(sketch);
        }
        {
            var Q0;
            Q0=sQuery(id+"F49.wireOp",VERTEX,"E86");
            var Q1;
            Q1=makeQuery(id+"F1.opExtrude","SWEPT_BODY",BODY,{"disambiguationData":[OSD([sQuery(id+"F0.wireOp",EDGE,"E0.bottom"),sQuery(id+"F0.wireOp",EDGE,"E0.top"),sQuery(id+"F0.wireOp",EDGE,"E0.left"),sQuery(id+"F0.wireOp",EDGE,"E0.right")])]});
            hole(context, id + "F50", {"style" : HoleStyle.SIMPLE, "endStyle" : HoleEndStyle.THROUGH, "holeDiameter" : 0.1 * mm, "startFromSketch" : true, "locations" : qUnion([Q0]), "scope" : qUnion([Q1]), "isTappedThrough" : true});
        }
        {
            var Q0;
            Q0=makeQuery(id+"F4.boolean.opBoolean","COPY",FACE,{"derivedFrom":makeQuery(id+"F4.opExtrude","CAP_FACE",FACE,{"disambiguationData":[OSD([sQuery(id+"F3.wireOp",EDGE,"E57.bottom"),sQuery(id+"F3.wireOp",EDGE,"E57.top"),sQuery(id+"F3.wireOp",EDGE,"E57.left"),sQuery(id+"F3.wireOp",EDGE,"E57.right")])],"isStart":false})});
            var sketch = newSketch(context, id + "F51", { "sketchPlane" : qUnion([Q0])});
            skPoint(sketch, "E87", {"position": v(7.5, -2.5) * mm});
            skSolve(sketch);
        }
        {
            var Q0;
            Q0=sQuery(id+"F51.wireOp",VERTEX,"E87");
            var Q1;
            Q1=makeQuery(id+"F1.opExtrude","SWEPT_BODY",BODY,{"disambiguationData":[OSD([sQuery(id+"F0.wireOp",EDGE,"E0.bottom"),sQuery(id+"F0.wireOp",EDGE,"E0.top"),sQuery(id+"F0.wireOp",EDGE,"E0.left"),sQuery(id+"F0.wireOp",EDGE,"E0.right")])]});
            hole(context, id + "F52", {"style" : HoleStyle.SIMPLE, "endStyle" : HoleEndStyle.THROUGH, "holeDiameter" : 0.1 * mm, "startFromSketch" : true, "locations" : qUnion([Q0]), "scope" : qUnion([Q1]), "isTappedThrough" : true});
        }
        {
            var Q0;
            Q0=makeQuery(id+"F4.boolean.opBoolean","COPY",FACE,{"derivedFrom":makeQuery(id+"F4.opExtrude","CAP_FACE",FACE,{"disambiguationData":[OSD([sQuery(id+"F3.wireOp",EDGE,"E63.bottom"),sQuery(id+"F3.wireOp",EDGE,"E63.top"),sQuery(id+"F3.wireOp",EDGE,"E63.left"),sQuery(id+"F3.wireOp",EDGE,"E63.right")])],"isStart":false})});
            var sketch = newSketch(context, id + "F53", { "sketchPlane" : qUnion([Q0])});
            skPoint(sketch, "E88", {"position": v(7.5, -5) * mm});
            skSolve(sketch);
        }
        {
            var Q0;
            Q0=sQuery(id+"F53.wireOp",VERTEX,"E88");
            var Q1;
            Q1=makeQuery(id+"F1.opExtrude","SWEPT_BODY",BODY,{"disambiguationData":[OSD([sQuery(id+"F0.wireOp",EDGE,"E0.bottom"),sQuery(id+"F0.wireOp",EDGE,"E0.top"),sQuery(id+"F0.wireOp",EDGE,"E0.left"),sQuery(id+"F0.wireOp",EDGE,"E0.right")])]});
            hole(context, id + "F54", {"style" : HoleStyle.SIMPLE, "endStyle" : HoleEndStyle.THROUGH, "holeDiameter" : 0.1 * mm, "startFromSketch" : true, "locations" : qUnion([Q0]), "scope" : qUnion([Q1]), "isTappedThrough" : true});
        }
        {
            var Q0;
            Q0=makeQuery(id+"F4.boolean.opBoolean","COPY",FACE,{"derivedFrom":makeQuery(id+"F4.opExtrude","CAP_FACE",FACE,{"disambiguationData":[OSD([sQuery(id+"F3.wireOp",EDGE,"E62.bottom"),sQuery(id+"F3.wireOp",EDGE,"E62.top"),sQuery(id+"F3.wireOp",EDGE,"E62.left"),sQuery(id+"F3.wireOp",EDGE,"E62.right")])],"isStart":false})});
            var sketch = newSketch(context, id + "F55", { "sketchPlane" : qUnion([Q0])});
            skPoint(sketch, "E89", {"position": v(4.5, -5) * mm});
            skSolve(sketch);
        }
        {
            var Q0;
            Q0=sQuery(id+"F55.wireOp",VERTEX,"E89");
            var Q1;
            Q1=makeQuery(id+"F1.opExtrude","SWEPT_BODY",BODY,{"disambiguationData":[OSD([sQuery(id+"F0.wireOp",EDGE,"E0.bottom"),sQuery(id+"F0.wireOp",EDGE,"E0.top"),sQuery(id+"F0.wireOp",EDGE,"E0.left"),sQuery(id+"F0.wireOp",EDGE,"E0.right")])]});
            hole(context, id + "F56", {"style" : HoleStyle.SIMPLE, "endStyle" : HoleEndStyle.THROUGH, "holeDiameter" : 0.1 * mm, "startFromSketch" : true, "locations" : qUnion([Q0]), "scope" : qUnion([Q1]), "isTappedThrough" : true});
        }
        {
            var Q0;
            Q0=makeQuery(id+"F4.boolean.opBoolean","COPY",FACE,{"derivedFrom":makeQuery(id+"F4.opExtrude","CAP_FACE",FACE,{"disambiguationData":[OSD([sQuery(id+"F3.wireOp",EDGE,"E61.bottom"),sQuery(id+"F3.wireOp",EDGE,"E61.top"),sQuery(id+"F3.wireOp",EDGE,"E61.left"),sQuery(id+"F3.wireOp",EDGE,"E61.right")])],"isStart":false})});
            var sketch = newSketch(context, id + "F57", { "sketchPlane" : qUnion([Q0])});
            skPoint(sketch, "E90", {"position": v(1.5, -5) * mm});
            skSolve(sketch);
        }
        {
            var Q0;
            Q0=sQuery(id+"F57.wireOp",VERTEX,"E90");
            var Q1;
            Q1=makeQuery(id+"F1.opExtrude","SWEPT_BODY",BODY,{"disambiguationData":[OSD([sQuery(id+"F0.wireOp",EDGE,"E0.bottom"),sQuery(id+"F0.wireOp",EDGE,"E0.top"),sQuery(id+"F0.wireOp",EDGE,"E0.left"),sQuery(id+"F0.wireOp",EDGE,"E0.right")])]});
            hole(context, id + "F58", {"style" : HoleStyle.SIMPLE, "endStyle" : HoleEndStyle.THROUGH, "holeDiameter" : 0.1 * mm, "startFromSketch" : true, "locations" : qUnion([Q0]), "scope" : qUnion([Q1]), "isTappedThrough" : true});
        }
        {
            var Q0;
            Q0=makeQuery(id+"F4.boolean.opBoolean","COPY",FACE,{"derivedFrom":makeQuery(id+"F4.opExtrude","CAP_FACE",FACE,{"disambiguationData":[OSD([sQuery(id+"F3.wireOp",EDGE,"E60.bottom"),sQuery(id+"F3.wireOp",EDGE,"E60.top"),sQuery(id+"F3.wireOp",EDGE,"E60.left"),sQuery(id+"F3.wireOp",EDGE,"E60.right")])],"isStart":false})});
            var sketch = newSketch(context, id + "F59", { "sketchPlane" : qUnion([Q0])});
            skPoint(sketch, "E91", {"position": v(-1.5, -5) * mm});
            skSolve(sketch);
        }
        {
            var Q0;
            Q0=sQuery(id+"F59.wireOp",VERTEX,"E91");
            var Q1;
            Q1=makeQuery(id+"F1.opExtrude","SWEPT_BODY",BODY,{"disambiguationData":[OSD([sQuery(id+"F0.wireOp",EDGE,"E0.bottom"),sQuery(id+"F0.wireOp",EDGE,"E0.top"),sQuery(id+"F0.wireOp",EDGE,"E0.left"),sQuery(id+"F0.wireOp",EDGE,"E0.right")])]});
            hole(context, id + "F60", {"style" : HoleStyle.SIMPLE, "endStyle" : HoleEndStyle.THROUGH, "holeDiameter" : 0.1 * mm, "startFromSketch" : true, "locations" : qUnion([Q0]), "scope" : qUnion([Q1]), "isTappedThrough" : true});
        }
        {
            var Q0;
            Q0=makeQuery(id+"F4.boolean.opBoolean","COPY",FACE,{"derivedFrom":makeQuery(id+"F4.opExtrude","CAP_FACE",FACE,{"disambiguationData":[OSD([sQuery(id+"F3.wireOp",EDGE,"E59.bottom"),sQuery(id+"F3.wireOp",EDGE,"E59.top"),sQuery(id+"F3.wireOp",EDGE,"E59.left"),sQuery(id+"F3.wireOp",EDGE,"E59.right")])],"isStart":false})});
            var sketch = newSketch(context, id + "F61", { "sketchPlane" : qUnion([Q0])});
            skPoint(sketch, "E92", {"position": v(-4.5, -5) * mm});
            skSolve(sketch);
        }
        {
            var Q0;
            Q0=sQuery(id+"F61.wireOp",VERTEX,"E92");
            var Q1;
            Q1=makeQuery(id+"F1.opExtrude","SWEPT_BODY",BODY,{"disambiguationData":[OSD([sQuery(id+"F0.wireOp",EDGE,"E0.bottom"),sQuery(id+"F0.wireOp",EDGE,"E0.top"),sQuery(id+"F0.wireOp",EDGE,"E0.left"),sQuery(id+"F0.wireOp",EDGE,"E0.right")])]});
            hole(context, id + "F62", {"style" : HoleStyle.SIMPLE, "endStyle" : HoleEndStyle.THROUGH, "holeDiameter" : 0.1 * mm, "startFromSketch" : true, "locations" : qUnion([Q0]), "scope" : qUnion([Q1]), "isTappedThrough" : true});
        }
        {
            var Q0;
            Q0=makeQuery(id+"F4.boolean.opBoolean","COPY",FACE,{"derivedFrom":makeQuery(id+"F4.opExtrude","CAP_FACE",FACE,{"disambiguationData":[OSD([sQuery(id+"F3.wireOp",EDGE,"E58.bottom"),sQuery(id+"F3.wireOp",EDGE,"E58.top"),sQuery(id+"F3.wireOp",EDGE,"E58.left"),sQuery(id+"F3.wireOp",EDGE,"E58.right")])],"isStart":false})});
            var sketch = newSketch(context, id + "F63", { "sketchPlane" : qUnion([Q0])});
            skPoint(sketch, "E93", {"position": v(-7.5, -5) * mm});
            skSolve(sketch);
        }
        {
            var Q0;
            Q0=sQuery(id+"F63.wireOp",VERTEX,"E93");
            var Q1;
            Q1=makeQuery(id+"F1.opExtrude","SWEPT_BODY",BODY,{"disambiguationData":[OSD([sQuery(id+"F0.wireOp",EDGE,"E0.bottom"),sQuery(id+"F0.wireOp",EDGE,"E0.top"),sQuery(id+"F0.wireOp",EDGE,"E0.left"),sQuery(id+"F0.wireOp",EDGE,"E0.right")])]});
            hole(context, id + "F64", {"style" : HoleStyle.SIMPLE, "endStyle" : HoleEndStyle.THROUGH, "holeDiameter" : 0.1 * mm, "startFromSketch" : true, "locations" : qUnion([Q0]), "scope" : qUnion([Q1]), "isTappedThrough" : true});
        }
    });
